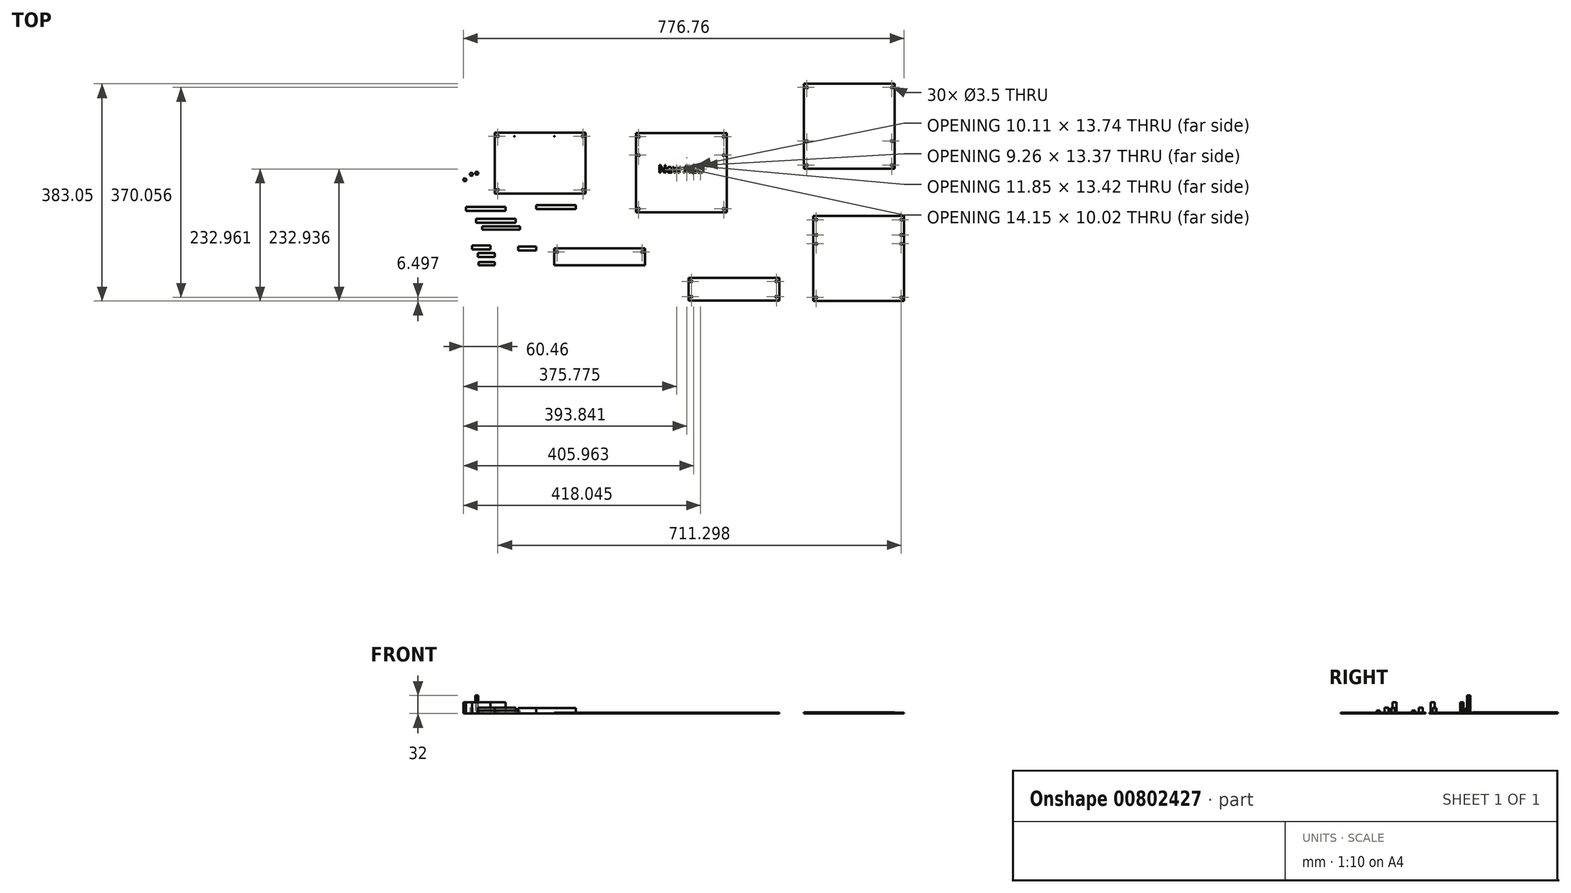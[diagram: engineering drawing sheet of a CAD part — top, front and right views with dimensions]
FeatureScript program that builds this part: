
annotation { "Feature Type Name" : "Feature", "Feature Type Description" : "" }
export const myFeature = defineFeature(function(context is Context, id is Id, definition is map)
    precondition{}
    {
        {
            var Q0;
            Q0=qCreatedBy(makeId("Top.planeOp"),FACE);
            var sketch = newSketch(context, id + "F0", { "sketchPlane" : qUnion([Q0])});
            skLineSegment(sketch, "E0.bottom", {"start": v(0, 0) * mm, "end": v(160, 0) * mm});
            skLineSegment(sketch, "E0.top", {"start": v(0, 107.5) * mm, "end": v(160, 107.5) * mm});
            skLineSegment(sketch, "E0.left", {"start": v(0, 0) * mm, "end": v(0, 107.5) * mm});
            skLineSegment(sketch, "E0.right", {"start": v(160, 0) * mm, "end": v(160, 107.5) * mm});
            skLineSegment(sketch, "E1", {"start": v(34.27, 115.15) * mm, "end": v(34.27, 89.45) * mm, "construction": true});
            skLineSegment(sketch, "E2", {"start": v(104.78, 115.15) * mm, "end": v(104.78, 86.57) * mm, "construction": true});
            skLineSegment(sketch, "E3.bottom", {"start": v(5, 101) * mm, "end": v(155, 101) * mm, "construction": true});
            skLineSegment(sketch, "E3.top", {"start": v(5, 6.5) * mm, "end": v(155, 6.5) * mm, "construction": true});
            skLineSegment(sketch, "E3.left", {"start": v(5, 101) * mm, "end": v(5, 6.5) * mm, "construction": true});
            skLineSegment(sketch, "E3.right", {"start": v(155, 101) * mm, "end": v(155, 6.5) * mm, "construction": true});
            skCircle(sketch, "E4", {"center": v(34.27, 101) * mm, "radius": 0.5 * mm});
            skCircle(sketch, "E5", {"center": v(104.78, 101) * mm, "radius": 0.5 * mm});
            skSolve(sketch);
        }
        {
            var Q0;
            Q0=makeQuery(id+"F0.imprint","IMPRINT",FACE,{"disambiguationData":[TD([[makeQuery(id+"F0.imprint","IMPRINT",EDGE,{"derivedFrom":sQuery(id+"F0.wireOp",EDGE,"E0.bottom")}),1.0]])]});
            extrude(context, id + "F1", {"entities" : qUnion([Q0]), "depth" : 1.6 * mm, "offsetDistance" : 25 * mm});
        }
        {
            var Q0;
            Q0=sQuery(id+"F0.wireOp",VERTEX,"E3.bottom.start");
            var Q1;
            Q1=sQuery(id+"F0.wireOp",VERTEX,"E3.bottom.end");
            var Q2;
            Q2=sQuery(id+"F0.wireOp",VERTEX,"E3.top.end");
            var Q3;
            Q3=sQuery(id+"F0.wireOp",VERTEX,"E3.top.start");
            var Q4;
            Q4=makeQuery(id+"F1.opExtrude","SWEPT_BODY",BODY,{"disambiguationData":[OSD([sQuery(id+"F0.wireOp",EDGE,"E0.bottom"),sQuery(id+"F0.wireOp",EDGE,"E0.top"),sQuery(id+"F0.wireOp",EDGE,"E0.left"),sQuery(id+"F0.wireOp",EDGE,"E0.right")])]});
            hole(context, id + "F2", {"style" : HoleStyle.SIMPLE, "endStyle" : HoleEndStyle.THROUGH, "oppositeDirection" : true, "holeDiameter" : 3.5 * mm, "majorDiameter" : 5 * mm, "isTappedThrough" : true, "tappedDepth" : 12 * mm, "tapClearance" : 3, "startFromSketch" : true, "locations" : qUnion([Q0, Q1, Q2, Q3]), "scope" : qUnion([Q4])});
        }
        {
            var Q0;
            Q0=qCreatedBy(makeId("Top.planeOp"),FACE);
            var sketch = newSketch(context, id + "F3", { "sketchPlane" : qUnion([Q0])});
            skLineSegment(sketch, "E6.bottom", {"start": v(-51.1, -23.64) * mm, "end": v(18.9, -23.64) * mm});
            skLineSegment(sketch, "E6.top", {"start": v(-51.1, -30.64) * mm, "end": v(18.9, -30.64) * mm});
            skLineSegment(sketch, "E6.left", {"start": v(-51.1, -23.64) * mm, "end": v(-51.1, -30.64) * mm});
            skLineSegment(sketch, "E6.right", {"start": v(18.9, -23.64) * mm, "end": v(18.9, -30.64) * mm});
            skSolve(sketch);
        }
        {
            var Q0;
            Q0=makeQuery(id+"F3.imprint","IMPRINT",FACE,{"disambiguationData":[TD([[makeQuery(id+"F3.imprint","IMPRINT",EDGE,{"derivedFrom":sQuery(id+"F3.wireOp",EDGE,"E6.bottom")}),-1.0]])]});
            extrude(context, id + "F4", {"entities" : qUnion([Q0]), "depth" : 20 * mm, "offsetDistance" : 25 * mm});
        }
        {
            var Q0;
            Q0=qCreatedBy(makeId("Top.planeOp"),FACE);
            var sketch = newSketch(context, id + "F5", { "sketchPlane" : qUnion([Q0])});
            skLineSegment(sketch, "E7.bottom", {"start": v(-33.26, -44.66) * mm, "end": v(36.74, -44.66) * mm});
            skLineSegment(sketch, "E7.top", {"start": v(-33.26, -51.66) * mm, "end": v(36.74, -51.66) * mm});
            skLineSegment(sketch, "E7.left", {"start": v(-33.26, -44.66) * mm, "end": v(-33.26, -51.66) * mm});
            skLineSegment(sketch, "E7.right", {"start": v(36.74, -44.66) * mm, "end": v(36.74, -51.66) * mm});
            skSolve(sketch);
        }
        {
            var Q0;
            Q0=makeQuery(id+"F5.imprint","IMPRINT",FACE,{"disambiguationData":[TD([[makeQuery(id+"F5.imprint","IMPRINT",EDGE,{"derivedFrom":sQuery(id+"F5.wireOp",EDGE,"E7.bottom")}),-1.0]])]});
            extrude(context, id + "F6", {"entities" : qUnion([Q0]), "depth" : 10.4 * mm, "offsetDistance" : 25 * mm});
        }
        {
            var Q0;
            Q0=qCreatedBy(makeId("Top.planeOp"),FACE);
            var sketch = newSketch(context, id + "F7", { "sketchPlane" : qUnion([Q0])});
            skLineSegment(sketch, "E8.bottom", {"start": v(-22.8, -58.18) * mm, "end": v(44.2, -58.18) * mm});
            skLineSegment(sketch, "E8.top", {"start": v(-22.8, -63.88) * mm, "end": v(44.2, -63.88) * mm});
            skLineSegment(sketch, "E8.left", {"start": v(-22.8, -58.18) * mm, "end": v(-22.8, -63.88) * mm});
            skLineSegment(sketch, "E8.right", {"start": v(44.2, -58.18) * mm, "end": v(44.2, -63.88) * mm});
            skSolve(sketch);
        }
        {
            var Q0;
            Q0=makeQuery(id+"F7.imprint","IMPRINT",FACE,{"disambiguationData":[TD([[makeQuery(id+"F7.imprint","IMPRINT",EDGE,{"derivedFrom":sQuery(id+"F7.wireOp",EDGE,"E8.bottom")}),-1.0]])]});
            extrude(context, id + "F8", {"entities" : qUnion([Q0]), "depth" : 5.5 * mm, "offsetDistance" : 25 * mm});
        }
        {
            var Q0;
            Q0=qCreatedBy(makeId("Top.planeOp"),FACE);
            var sketch = newSketch(context, id + "F9", { "sketchPlane" : qUnion([Q0])});
            skLineSegment(sketch, "E9.bottom", {"start": v(72.56, -20.42) * mm, "end": v(142.56, -20.42) * mm});
            skLineSegment(sketch, "E9.top", {"start": v(72.56, -27.42) * mm, "end": v(142.56, -27.42) * mm});
            skLineSegment(sketch, "E9.left", {"start": v(72.56, -20.42) * mm, "end": v(72.56, -27.42) * mm});
            skLineSegment(sketch, "E9.right", {"start": v(142.56, -20.42) * mm, "end": v(142.56, -27.42) * mm});
            skSolve(sketch);
        }
        {
            var Q0;
            Q0=makeQuery(id+"F9.imprint","IMPRINT",FACE,{"disambiguationData":[TD([[makeQuery(id+"F9.imprint","IMPRINT",EDGE,{"derivedFrom":sQuery(id+"F9.wireOp",EDGE,"E9.bottom")}),-1.0]])]});
            extrude(context, id + "F10", {"entities" : qUnion([Q0]), "depth" : 9.8 * mm, "offsetDistance" : 25 * mm});
        }
        {
            var Q0;
            Q0=qCreatedBy(makeId("Top.planeOp"),FACE);
            var sketch = newSketch(context, id + "F11", { "sketchPlane" : qUnion([Q0])});
            skLineSegment(sketch, "E10.bottom", {"start": v(-40, -91.42) * mm, "end": v(-8, -91.42) * mm});
            skLineSegment(sketch, "E10.top", {"start": v(-40, -98.42) * mm, "end": v(-8, -98.42) * mm});
            skLineSegment(sketch, "E10.left", {"start": v(-40, -91.42) * mm, "end": v(-40, -98.42) * mm});
            skLineSegment(sketch, "E10.right", {"start": v(-8, -91.42) * mm, "end": v(-8, -98.42) * mm});
            skSolve(sketch);
        }
        {
            var Q0;
            Q0=makeQuery(id+"F11.imprint","IMPRINT",FACE,{"disambiguationData":[TD([[makeQuery(id+"F11.imprint","IMPRINT",EDGE,{"derivedFrom":sQuery(id+"F11.wireOp",EDGE,"E10.bottom")}),-1.0]])]});
            extrude(context, id + "F12", {"entities" : qUnion([Q0]), "depth" : 20 * mm, "offsetDistance" : 25 * mm});
        }
        {
            var Q0;
            Q0=qCreatedBy(makeId("Top.planeOp"),FACE);
            var sketch = newSketch(context, id + "F13", { "sketchPlane" : qUnion([Q0])});
            skLineSegment(sketch, "E11.bottom", {"start": v(-30, -105.14) * mm, "end": v(0, -105.14) * mm});
            skLineSegment(sketch, "E11.top", {"start": v(-30, -112.14) * mm, "end": v(0, -112.14) * mm});
            skLineSegment(sketch, "E11.left", {"start": v(-30, -105.14) * mm, "end": v(-30, -112.14) * mm});
            skLineSegment(sketch, "E11.right", {"start": v(0, -105.14) * mm, "end": v(0, -112.14) * mm});
            skSolve(sketch);
        }
        {
            var Q0;
            Q0=makeQuery(id+"F13.imprint","IMPRINT",FACE,{"disambiguationData":[TD([[makeQuery(id+"F13.imprint","IMPRINT",EDGE,{"derivedFrom":sQuery(id+"F13.wireOp",EDGE,"E11.bottom")}),-1.0]])]});
            extrude(context, id + "F14", {"entities" : qUnion([Q0]), "depth" : 10.4 * mm, "offsetDistance" : 25 * mm});
        }
        {
            var Q0;
            Q0=qCreatedBy(makeId("Top.planeOp"),FACE);
            var sketch = newSketch(context, id + "F15", { "sketchPlane" : qUnion([Q0])});
            skLineSegment(sketch, "E12.bottom", {"start": v(-29, -120.64) * mm, "end": v(0, -120.64) * mm});
            skLineSegment(sketch, "E12.top", {"start": v(-29, -126.34) * mm, "end": v(0, -126.34) * mm});
            skLineSegment(sketch, "E12.left", {"start": v(-29, -120.64) * mm, "end": v(-29, -126.34) * mm});
            skLineSegment(sketch, "E12.right", {"start": v(0, -120.64) * mm, "end": v(0, -126.34) * mm});
            skSolve(sketch);
        }
        {
            var Q0;
            Q0=makeQuery(id+"F15.imprint","IMPRINT",FACE,{"disambiguationData":[TD([[makeQuery(id+"F15.imprint","IMPRINT",EDGE,{"derivedFrom":sQuery(id+"F15.wireOp",EDGE,"E12.bottom")}),-1.0]])]});
            extrude(context, id + "F16", {"entities" : qUnion([Q0]), "depth" : 5.5 * mm, "offsetDistance" : 25 * mm});
        }
        {
            var Q0;
            Q0=qCreatedBy(makeId("Top.planeOp"),FACE);
            var sketch = newSketch(context, id + "F17", { "sketchPlane" : qUnion([Q0])});
            skLineSegment(sketch, "E13.bottom", {"start": v(41.03, -93.71) * mm, "end": v(73.03, -93.71) * mm});
            skLineSegment(sketch, "E13.top", {"start": v(41.03, -100.71) * mm, "end": v(73.03, -100.71) * mm});
            skLineSegment(sketch, "E13.left", {"start": v(41.03, -93.71) * mm, "end": v(41.03, -100.71) * mm});
            skLineSegment(sketch, "E13.right", {"start": v(73.03, -93.71) * mm, "end": v(73.03, -100.71) * mm});
            skSolve(sketch);
        }
        {
            var Q0;
            Q0=makeQuery(id+"F17.imprint","IMPRINT",FACE,{"disambiguationData":[TD([[makeQuery(id+"F17.imprint","IMPRINT",EDGE,{"derivedFrom":sQuery(id+"F17.wireOp",EDGE,"E13.bottom")}),-1.0]])]});
            extrude(context, id + "F18", {"entities" : qUnion([Q0]), "depth" : 9.8 * mm, "offsetDistance" : 25 * mm});
        }
        {
            var Q0;
            Q0=qCreatedBy(makeId("Top.planeOp"),FACE);
            var sketch = newSketch(context, id + "F19", { "sketchPlane" : qUnion([Q0])});
            skCircle(sketch, "E14.cCircle", {"center": v(-52.9, 24.26) * mm, "radius": 2.5 * mm, "construction": true});
            skLineSegment(sketch, "E14.0", {"start": v(-52.82, 27.15) * mm, "end": v(-50.36, 25.63) * mm});
            skLineSegment(sketch, "E14.1", {"start": v(-50.36, 25.63) * mm, "end": v(-50.46, 22.74) * mm});
            skLineSegment(sketch, "E14.2", {"start": v(-50.46, 22.74) * mm, "end": v(-53, 21.38) * mm});
            skLineSegment(sketch, "E14.3", {"start": v(-53, 21.38) * mm, "end": v(-55.46, 22.9) * mm});
            skLineSegment(sketch, "E14.4", {"start": v(-55.46, 22.9) * mm, "end": v(-55.36, 25.79) * mm});
            skLineSegment(sketch, "E14.5", {"start": v(-55.36, 25.79) * mm, "end": v(-52.82, 27.15) * mm});
            skPoint(sketch, "E14.0.midPoint", {"position": v(-51.59, 26.39) * mm});
            skSolve(sketch);
        }
        {
            var Q0;
            Q0=makeQuery(id+"F19.imprint","IMPRINT",FACE,{"disambiguationData":[TD([[makeQuery(id+"F19.imprint","IMPRINT",EDGE,{"derivedFrom":sQuery(id+"F19.wireOp",EDGE,"E14.0")}),-1.0]])]});
            extrude(context, id + "F20", {"entities" : qUnion([Q0]), "depth" : 20 * mm, "offsetDistance" : 25 * mm});
        }
        {
            var Q0;
            Q0=qCreatedBy(makeId("Top.planeOp"),FACE);
            var sketch = newSketch(context, id + "F21", { "sketchPlane" : qUnion([Q0])});
            skLineSegment(sketch, "E15.bottom", {"start": v(104.6, -96.45) * mm, "end": v(264.6, -96.45) * mm});
            skLineSegment(sketch, "E15.top", {"start": v(104.6, -126.45) * mm, "end": v(264.6, -126.45) * mm});
            skLineSegment(sketch, "E15.left", {"start": v(104.6, -96.45) * mm, "end": v(104.6, -126.45) * mm});
            skLineSegment(sketch, "E15.right", {"start": v(264.6, -96.45) * mm, "end": v(264.6, -126.45) * mm});
            skCircle(sketch, "E16", {"center": v(109.6, -102.95) * mm, "radius": 1.75 * mm});
            skCircle(sketch, "E17", {"center": v(259.6, -102.95) * mm, "radius": 1.75 * mm});
            skSolve(sketch);
        }
        {
            var Q0;
            Q0=makeQuery(id+"F21.imprint","IMPRINT",FACE,{"disambiguationData":[TD([[makeQuery(id+"F21.imprint","IMPRINT",EDGE,{"derivedFrom":sQuery(id+"F21.wireOp",EDGE,"E15.bottom")}),-1.0]])]});
            extrude(context, id + "F22", {"entities" : qUnion([Q0]), "depth" : 1.6 * mm, "offsetDistance" : 25 * mm});
        }
        {
            var Q0;
            Q0=qCreatedBy(makeId("Top.planeOp"),FACE);
            var sketch = newSketch(context, id + "F23", { "sketchPlane" : qUnion([Q0])});
            skLineSegment(sketch, "E18.bottom", {"start": v(248.41, 106.6) * mm, "end": v(408.41, 106.6) * mm});
            skLineSegment(sketch, "E18.top", {"start": v(248.41, -33.4) * mm, "end": v(408.41, -33.4) * mm});
            skLineSegment(sketch, "E18.left", {"start": v(248.41, 106.6) * mm, "end": v(248.41, -33.4) * mm});
            skLineSegment(sketch, "E18.right", {"start": v(408.41, 106.6) * mm, "end": v(408.41, -33.4) * mm});
            skCircle(sketch, "E19", {"center": v(253.41, 100.1) * mm, "radius": 1.75 * mm});
            skCircle(sketch, "E20", {"center": v(403.41, 100.1) * mm, "radius": 1.75 * mm});
            skCircle(sketch, "E21", {"center": v(253.41, 67.6) * mm, "radius": 1.75 * mm});
            skCircle(sketch, "E22", {"center": v(403.41, 67.6) * mm, "radius": 1.75 * mm});
            skCircle(sketch, "E23", {"center": v(253.41, -26.9) * mm, "radius": 1.75 * mm});
            skCircle(sketch, "E24", {"center": v(403.41, -26.9) * mm, "radius": 1.75 * mm});
            skText(sketch, "E25", { "text": "New ACB", "fontName": "OpenSans-Regular.ttf"});
            const initialGuessF23  = {"E25": [0.28841, 0.03663, 1, 0, 0.01348]};
            skSetInitialGuess(sketch, initialGuessF23);
            skSolve(sketch);
        }
        {
            var Q0;
            Q0=makeQuery(id+"F23.imprint","IMPRINT",FACE,{"disambiguationData":[TD([[makeQuery(id+"F23.imprint","IMPRINT",EDGE,{"derivedFrom":sQuery(id+"F23.wireOp",EDGE,"E18.bottom")}),-1.0]])]});
            extrude(context, id + "F24", {"entities" : qUnion([Q0]), "depth" : 1.6 * mm, "offsetDistance" : 25 * mm});
        }
        {
            var Q0;
            Q0=qCreatedBy(makeId("Top.planeOp"),FACE);
            var sketch = newSketch(context, id + "F25", { "sketchPlane" : qUnion([Q0])});
            skCircle(sketch, "E26.cCircle", {"center": v(-41.73, 33.8) * mm, "radius": 2.5 * mm, "construction": true});
            skLineSegment(sketch, "E26.0", {"start": v(-39.25, 32.34) * mm, "end": v(-41.76, 30.91) * mm});
            skLineSegment(sketch, "E26.1", {"start": v(-41.76, 30.91) * mm, "end": v(-44.25, 32.38) * mm});
            skLineSegment(sketch, "E26.2", {"start": v(-44.25, 32.38) * mm, "end": v(-44.22, 35.26) * mm});
            skLineSegment(sketch, "E26.3", {"start": v(-44.22, 35.26) * mm, "end": v(-41.71, 36.69) * mm});
            skLineSegment(sketch, "E26.4", {"start": v(-41.71, 36.69) * mm, "end": v(-39.22, 35.22) * mm});
            skLineSegment(sketch, "E26.5", {"start": v(-39.22, 35.22) * mm, "end": v(-39.25, 32.34) * mm});
            skPoint(sketch, "E26.0.midPoint", {"position": v(-40.5, 31.63) * mm});
            skSolve(sketch);
        }
        {
            var Q0;
            Q0=makeQuery(id+"F25.imprint","IMPRINT",FACE,{"disambiguationData":[TD([[makeQuery(id+"F25.imprint","IMPRINT",EDGE,{"derivedFrom":sQuery(id+"F25.wireOp",EDGE,"E26.0")}),-1.0]])]});
            extrude(context, id + "F26", {"entities" : qUnion([Q0]), "depth" : 10 * mm, "offsetDistance" : 25 * mm});
        }
        {
            var Q0;
            Q0=qCreatedBy(makeId("Top.planeOp"),FACE);
            var sketch = newSketch(context, id + "F27", { "sketchPlane" : qUnion([Q0])});
            skCircle(sketch, "E27.cCircle", {"center": v(-32.14, 35.9) * mm, "radius": 2.5 * mm, "construction": true});
            skLineSegment(sketch, "E27.0", {"start": v(-29.63, 34.48) * mm, "end": v(-32.12, 33.02) * mm});
            skLineSegment(sketch, "E27.1", {"start": v(-32.12, 33.02) * mm, "end": v(-34.63, 34.45) * mm});
            skLineSegment(sketch, "E27.2", {"start": v(-34.63, 34.45) * mm, "end": v(-34.65, 37.33) * mm});
            skLineSegment(sketch, "E27.3", {"start": v(-34.65, 37.33) * mm, "end": v(-32.15, 38.8) * mm});
            skLineSegment(sketch, "E27.4", {"start": v(-32.15, 38.8) * mm, "end": v(-29.65, 37.36) * mm});
            skLineSegment(sketch, "E27.5", {"start": v(-29.65, 37.36) * mm, "end": v(-29.63, 34.48) * mm});
            skPoint(sketch, "E27.0.midPoint", {"position": v(-30.88, 33.75) * mm});
            skSolve(sketch);
        }
        {
            var Q0;
            Q0=makeQuery(id+"F27.imprint","IMPRINT",FACE,{"disambiguationData":[TD([[makeQuery(id+"F27.imprint","IMPRINT",EDGE,{"derivedFrom":sQuery(id+"F27.wireOp",EDGE,"E27.0")}),-1.0]])]});
            extrude(context, id + "F28", {"entities" : qUnion([Q0]), "depth" : 32 * mm, "offsetDistance" : 25 * mm});
        }
        {
            var Q0;
            Q0=qCreatedBy(makeId("Top.planeOp"),FACE);
            var sketch = newSketch(context, id + "F29", { "sketchPlane" : qUnion([Q0])});
            skLineSegment(sketch, "E28.bottom", {"start": v(341.16, -148.37) * mm, "end": v(501.16, -148.37) * mm});
            skLineSegment(sketch, "E28.top", {"start": v(341.16, -188.37) * mm, "end": v(501.16, -188.37) * mm});
            skLineSegment(sketch, "E28.left", {"start": v(341.16, -148.37) * mm, "end": v(341.16, -188.37) * mm});
            skLineSegment(sketch, "E28.right", {"start": v(501.16, -148.37) * mm, "end": v(501.16, -188.37) * mm});
            skCircle(sketch, "E29", {"center": v(346.16, -154.87) * mm, "radius": 1.75 * mm});
            skCircle(sketch, "E30", {"center": v(346.16, -181.87) * mm, "radius": 1.75 * mm});
            skCircle(sketch, "E31", {"center": v(496.16, -154.87) * mm, "radius": 1.75 * mm});
            skCircle(sketch, "E32", {"center": v(496.16, -181.87) * mm, "radius": 1.75 * mm});
            skSolve(sketch);
        }
        {
            var Q0;
            Q0=qCreatedBy(makeId("Top.planeOp"),FACE);
            var sketch = newSketch(context, id + "F30", { "sketchPlane" : qUnion([Q0])});
            skLineSegment(sketch, "E33.bottom", {"start": v(561.3, -39.62) * mm, "end": v(721.3, -39.62) * mm});
            skLineSegment(sketch, "E33.top", {"start": v(561.3, -189.62) * mm, "end": v(721.3, -189.62) * mm});
            skLineSegment(sketch, "E33.left", {"start": v(561.3, -39.62) * mm, "end": v(561.3, -189.62) * mm});
            skLineSegment(sketch, "E33.right", {"start": v(721.3, -39.62) * mm, "end": v(721.3, -189.62) * mm});
            skCircle(sketch, "E34", {"center": v(566.3, -183.12) * mm, "radius": 1.75 * mm});
            skCircle(sketch, "E35", {"center": v(716.3, -183.12) * mm, "radius": 1.75 * mm});
            skCircle(sketch, "E36", {"center": v(566.3, -88.62) * mm, "radius": 1.75 * mm});
            skCircle(sketch, "E37", {"center": v(716.3, -88.62) * mm, "radius": 1.75 * mm});
            skCircle(sketch, "E38", {"center": v(566.3, -73.12) * mm, "radius": 1.75 * mm});
            skCircle(sketch, "E39", {"center": v(716.3, -73.12) * mm, "radius": 1.75 * mm});
            skCircle(sketch, "E40", {"center": v(716.3, -46.12) * mm, "radius": 1.75 * mm});
            skCircle(sketch, "E41", {"center": v(566.3, -46.12) * mm, "radius": 1.75 * mm});
            skSolve(sketch);
        }
        {
            var Q0;
            Q0=makeQuery(id+"F29.imprint","IMPRINT",FACE,{"disambiguationData":[TD([[makeQuery(id+"F29.imprint","IMPRINT",EDGE,{"derivedFrom":sQuery(id+"F29.wireOp",EDGE,"E28.bottom")}),-1.0]])]});
            extrude(context, id + "F31", {"entities" : qUnion([Q0]), "depth" : 1.6 * mm, "offsetDistance" : 25 * mm});
        }
        {
            var Q0;
            Q0=makeQuery(id+"F30.imprint","IMPRINT",FACE,{"disambiguationData":[TD([[makeQuery(id+"F30.imprint","IMPRINT",EDGE,{"derivedFrom":sQuery(id+"F30.wireOp",EDGE,"E33.bottom")}),-1.0]])]});
            extrude(context, id + "F32", {"entities" : qUnion([Q0]), "depth" : 1.6 * mm, "offsetDistance" : 25 * mm});
        }
        {
            var Q0;
            Q0=qCreatedBy(makeId("Top.planeOp"),FACE);
            var sketch = newSketch(context, id + "F33", { "sketchPlane" : qUnion([Q0])});
            skLineSegment(sketch, "E42.bottom", {"start": v(544.74, 193.43) * mm, "end": v(704.74, 193.43) * mm});
            skLineSegment(sketch, "E42.top", {"start": v(544.74, 43.43) * mm, "end": v(704.74, 43.43) * mm});
            skLineSegment(sketch, "E42.left", {"start": v(544.74, 193.43) * mm, "end": v(544.74, 43.43) * mm});
            skLineSegment(sketch, "E42.right", {"start": v(704.74, 193.43) * mm, "end": v(704.74, 43.43) * mm});
            skSolve(sketch);
        }
        {
            var Q0;
            Q0=makeQuery(id+"F33.imprint","IMPRINT",FACE,{"disambiguationData":[TD([[makeQuery(id+"F33.imprint","IMPRINT",EDGE,{"derivedFrom":sQuery(id+"F33.wireOp",EDGE,"E42.bottom")}),-1.0]])]});
            extrude(context, id + "F34", {"entities" : qUnion([Q0]), "depth" : 2 * mm, "offsetDistance" : 25 * mm});
        }
        {
            var Q0;
            Q0=makeQuery(id+"F34.opExtrude","CAP_FACE",FACE,{"disambiguationData":[OSD([sQuery(id+"F33.wireOp",EDGE,"E42.bottom"),sQuery(id+"F33.wireOp",EDGE,"E42.top"),sQuery(id+"F33.wireOp",EDGE,"E42.left"),sQuery(id+"F33.wireOp",EDGE,"E42.right")])],"isStart":false});
            var sketch = newSketch(context, id + "F35", { "sketchPlane" : qUnion([Q0])});
            skCircle(sketch, "E43", {"center": v(549.74, 186.93) * mm, "radius": 1.75 * mm});
            skCircle(sketch, "E44", {"center": v(549.74, 49.93) * mm, "radius": 1.75 * mm});
            skCircle(sketch, "E45", {"center": v(699.74, 186.93) * mm, "radius": 1.75 * mm});
            skCircle(sketch, "E46", {"center": v(699.74, 49.93) * mm, "radius": 1.75 * mm});
            skCircle(sketch, "E47", {"center": v(549.74, 92.43) * mm, "radius": 1.75 * mm});
            skCircle(sketch, "E48", {"center": v(699.74, 92.43) * mm, "radius": 1.75 * mm});
            skSolve(sketch);
        }
        {
            var Q0;
            Q0=makeQuery(id+"F35.imprint","IMPRINT",FACE,{"disambiguationData":[TD([[makeQuery(id+"F35.imprint","IMPRINT",EDGE,{"derivedFrom":sQuery(id+"F35.wireOp",EDGE,"E43")}),1.0]])]});
            var Q1;
            Q1=makeQuery(id+"F35.imprint","IMPRINT",FACE,{"disambiguationData":[TD([[makeQuery(id+"F35.imprint","IMPRINT",EDGE,{"derivedFrom":sQuery(id+"F35.wireOp",EDGE,"E45")}),1.0]])]});
            var Q2;
            Q2=makeQuery(id+"F35.imprint","IMPRINT",FACE,{"disambiguationData":[TD([[makeQuery(id+"F35.imprint","IMPRINT",EDGE,{"derivedFrom":sQuery(id+"F35.wireOp",EDGE,"E47")}),1.0]])]});
            var Q3;
            Q3=makeQuery(id+"F35.imprint","IMPRINT",FACE,{"disambiguationData":[TD([[makeQuery(id+"F35.imprint","IMPRINT",EDGE,{"derivedFrom":sQuery(id+"F35.wireOp",EDGE,"E48")}),1.0]])]});
            var Q4;
            Q4=makeQuery(id+"F35.imprint","IMPRINT",FACE,{"disambiguationData":[TD([[makeQuery(id+"F35.imprint","IMPRINT",EDGE,{"derivedFrom":sQuery(id+"F35.wireOp",EDGE,"E44")}),1.0]])]});
            var Q5;
            Q5=makeQuery(id+"F35.imprint","IMPRINT",FACE,{"disambiguationData":[TD([[makeQuery(id+"F35.imprint","IMPRINT",EDGE,{"derivedFrom":sQuery(id+"F35.wireOp",EDGE,"E46")}),1.0]])]});
            var Q6;
            Q6=sQuery(id+"F35.wireOp",EDGE,"E43");
            extrude(context, id + "F36", {"entities" : qUnion([Q0, Q1, Q2, Q3, Q4, Q5]), "operationType" : NewBodyOperationType.REMOVE, "surfaceEntities" : qUnion([Q6]), "oppositeDirection" : true, "depth" : 25 * mm, "offsetDistance" : 25 * mm});
        }
    });
